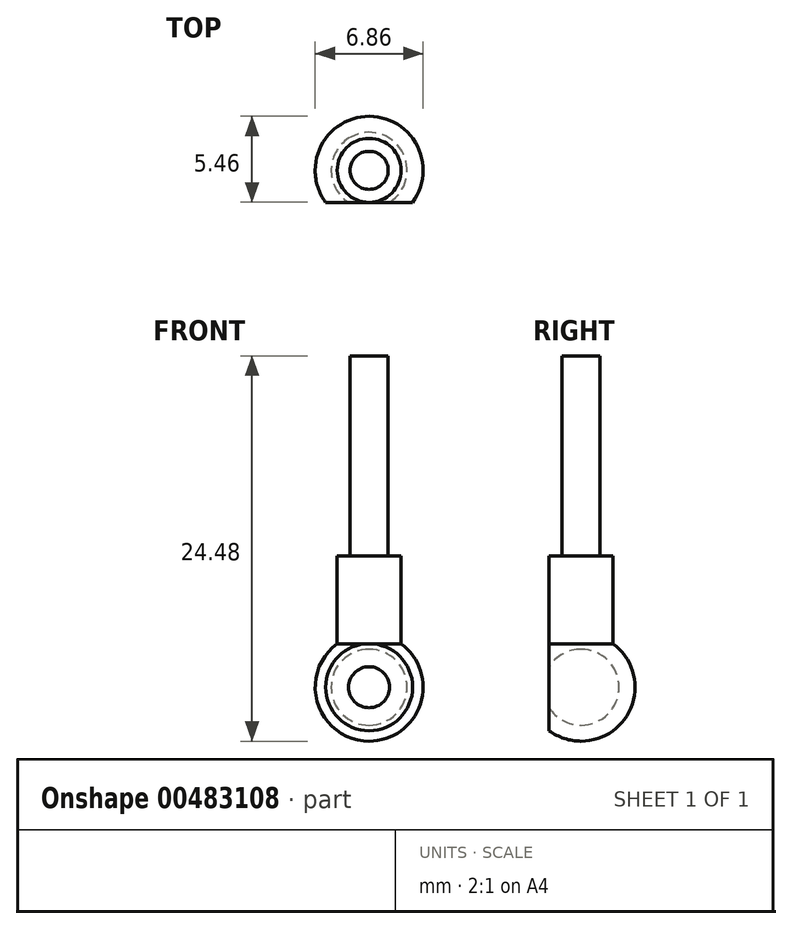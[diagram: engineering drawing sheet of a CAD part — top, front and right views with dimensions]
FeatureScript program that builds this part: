
annotation { "Feature Type Name" : "Feature", "Feature Type Description" : "" }
export const myFeature = defineFeature(function(context is Context, id is Id, definition is map)
    precondition{}
    {
        {
            var Q0;
            Q0=qCreatedBy(makeId("Front.planeOp"),FACE);
            var sketch = newSketch(context, id + "F0", { "sketchPlane" : qUnion([Q0])});
            skLineSegment(sketch, "E0", {"start": v(1.2, 18.29) * mm, "end": v(1.2, 5.59) * mm});
            skLineSegment(sketch, "E1", {"start": v(1.2, 5.59) * mm, "end": v(2.03, 5.59) * mm});
            skLineSegment(sketch, "E2", {"start": v(2.03, 5.59) * mm, "end": v(2.03, 0) * mm});
            skArc(sketch, "E3", {"start": v(0, -6.2) * mm, "mid": v(3.26, -3.83) * mm, "end": v(2.03, 0) * mm});
            skArc(sketch, "E4", {"start": v(0, -5.18) * mm, "mid": v(2.41, -2.76) * mm, "end": v(0, -0.35) * mm});
            skLineSegment(sketch, "E5.trimOffspring", {"start": v(0, -5.18) * mm, "end": v(0, -6.2) * mm});
            skLineSegment(sketch, "E6", {"start": v(1.2, 18.29) * mm, "end": v(0, 18.29) * mm});
            skLineSegment(sketch, "E7", {"start": v(0, -0.35) * mm, "end": v(0, 18.29) * mm});
            skLineSegment(sketch, "E8", {"start": v(0, -9.31) * mm, "end": v(0, 23.6) * mm, "construction": true});
            skSolve(sketch);
        }
        {
            var Q0;
            Q0=qSketchRegion(id+"F0",true);
            var Q1;
            Q1=sQuery(id+"F0.wireOp",EDGE,"E8");
            revolve(context, id + "F1", {"entities" : qUnion([Q0]), "axis" : qUnion([Q1]), "revolveType" : RevolveType.FULL});
        }
        {
            var Q0;
            Q0=qCreatedBy(makeId("Right.planeOp"),FACE);
            var sketch = newSketch(context, id + "F2", { "sketchPlane" : qUnion([Q0])});
            skLineSegment(sketch, "E9", {"start": v(-2.03, 0) * mm, "end": v(-2.03, 5.59) * mm});
            skLineSegment(sketch, "E10", {"start": v(-2.03, 0) * mm, "end": v(-2.03, -7.62) * mm});
            skLineSegment(sketch, "E11", {"start": v(-2.03, -7.62) * mm, "end": v(-5.2, -7.62) * mm});
            skLineSegment(sketch, "E12", {"start": v(-5.2, -7.62) * mm, "end": v(-5.2, 5.59) * mm});
            skLineSegment(sketch, "E13", {"start": v(-2.03, 5.59) * mm, "end": v(-5.2, 5.59) * mm});
            skSolve(sketch);
        }
        {
            var Q0;
            Q0=qSketchRegion(id+"F2",true);
            extrude(context, id + "F3", {"entities" : qUnion([Q0]), "operationType" : NewBodyOperationType.REMOVE, "endBound" : BoundingType.THROUGH_ALL, "depth" : 25.4 * mm, "hasSecondDirection" : true, "secondDirectionBound" : SecondDirectionBoundingType.THROUGH_ALL, "secondDirectionOppositeDirection" : true, "secondDirectionDepth" : 25.4 * mm});
        }
    });
